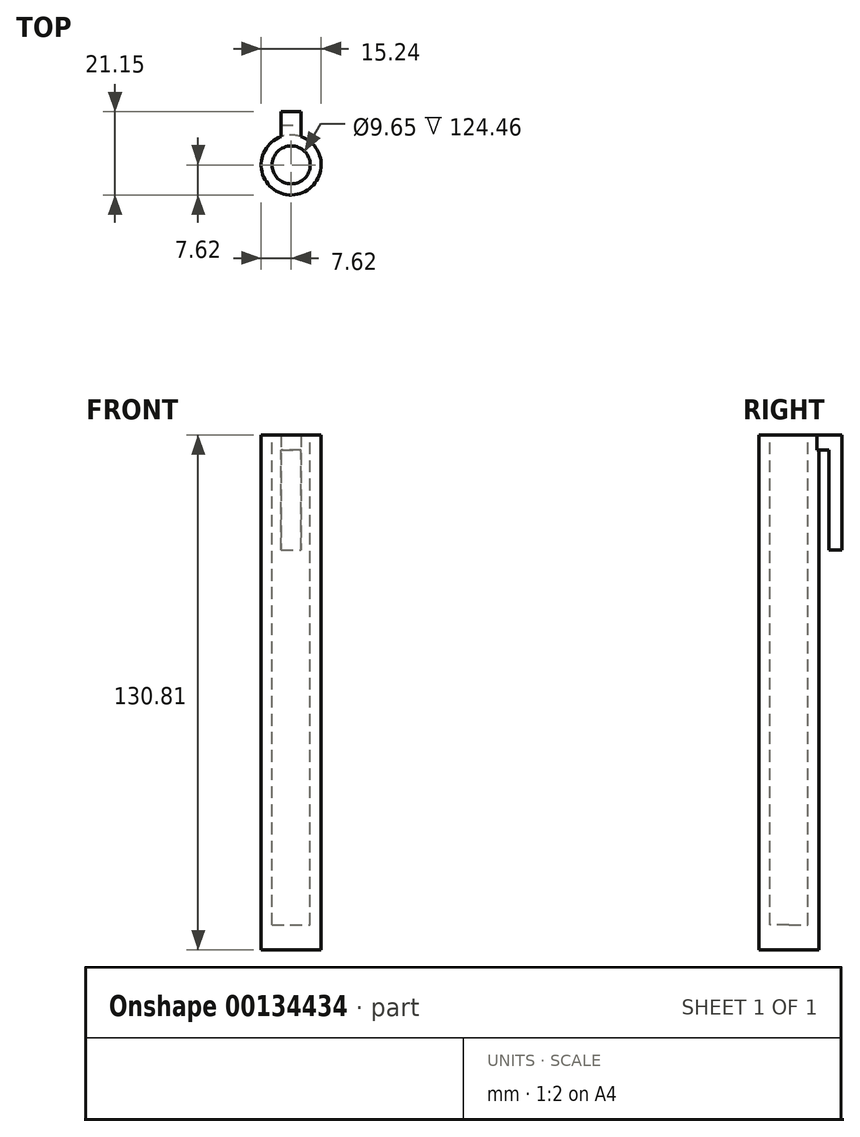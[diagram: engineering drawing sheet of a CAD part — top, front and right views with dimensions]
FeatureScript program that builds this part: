
annotation { "Feature Type Name" : "Feature", "Feature Type Description" : "" }
export const myFeature = defineFeature(function(context is Context, id is Id, definition is map)
    precondition{}
    {
        {
            var Q0;
            Q0=qCreatedBy(makeId("Top.planeOp"),FACE);
            var sketch = newSketch(context, id + "F0", { "sketchPlane" : qUnion([Q0])});
            skCircle(sketch, "E0", {"center": v(0, 0) * mm, "radius": 4.83 * mm});
            skCircle(sketch, "E1", {"center": v(0, 0) * mm, "radius": 7.62 * mm});
            skLineSegment(sketch, "E2", {"start": v(-2.54, 7.18) * mm, "end": v(-2.54, 13.53) * mm});
            skLineSegment(sketch, "E3", {"start": v(-2.54, 13.53) * mm, "end": v(2.54, 13.53) * mm});
            skLineSegment(sketch, "E4", {"start": v(2.54, 13.53) * mm, "end": v(2.54, 7.18) * mm});
            skLineSegment(sketch, "E5", {"start": v(-2.54, 10.16) * mm, "end": v(2.54, 10.16) * mm});
            skLineSegment(sketch, "E6", {"start": v(0, 13.53) * mm, "end": v(0, 0) * mm, "construction": true});
            skSolve(sketch);
        }
        {
            var Q0;
            Q0=makeQuery(id+"F0.imprint","IMPRINT",FACE,{"disambiguationData":[TD([[makeQuery(id+"F0.imprint","IMPRINT",EDGE,{"derivedFrom":sQuery(id+"F0.wireOp",EDGE,"E0")}),-1.0]])]});
            extrude(context, id + "F1", {"entities" : qUnion([Q0]), "oppositeDirection" : true, "depth" : 127 * mm});
        }
        {
            var Q0;
            Q0 = qSketchRegion(id + "F0", true);
            extrude(context, id + "F2", {"entities" : qUnion([Q0]), "operationType" : NewBodyOperationType.ADD, "depth" : 3.8 * mm});
        }
        {
            var Q0;
            {var subQ0=sQuery(id+"F0.wireOp",EDGE,"E3");Q0=makeQuery(id+"F0.imprint","IMPRINT",FACE,{"disambiguationData":[TD([[makeQuery(id+"F0.imprint","IMPRINT",EDGE,{"derivedFrom":subQ0}),-1.0]])]});}
            extrude(context, id + "F3", {"entities" : qUnion([Q0]), "operationType" : NewBodyOperationType.ADD, "oppositeDirection" : true, "depth" : 25.4 * mm});
        }
        {
            var Q0;
            Q0=makeQuery(id+"F1.opExtrude","CAP_FACE",FACE,{"disambiguationData":[OSD([sQuery(id+"F0.wireOp",EDGE,"E0"),sQuery(id+"F0.wireOp",EDGE,"E1")])],"isStart":false});
            var sketch = newSketch(context, id + "F4", { "sketchPlane" : qUnion([Q0])});
            skCircle(sketch, "E7", {"center": v(0, 0) * mm, "radius": 4.83 * mm});
            skSolve(sketch);
        }
        {
            var Q0;
            Q0 = qSketchRegion(id + "F4", true);
            extrude(context, id + "F5", {"entities" : qUnion([Q0]), "operationType" : NewBodyOperationType.ADD, "oppositeDirection" : true, "depth" : 6.35 * mm});
        }
    });
